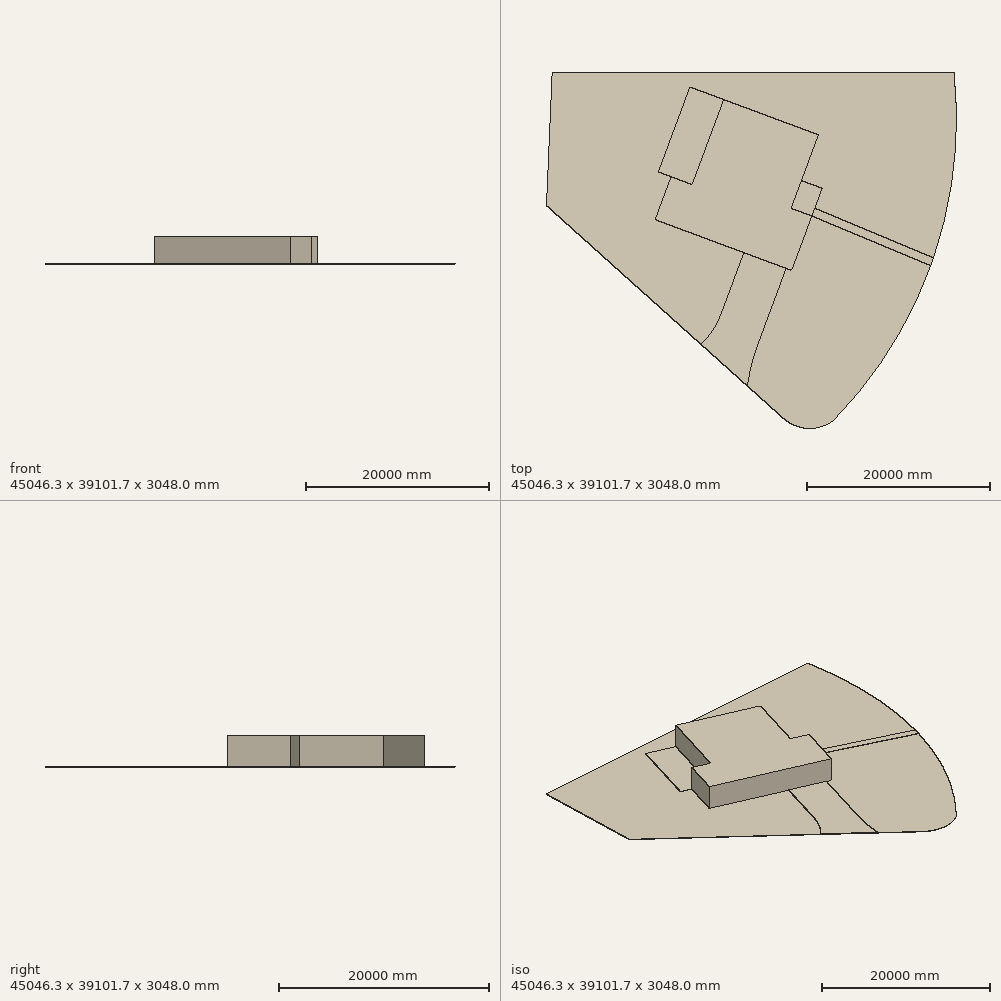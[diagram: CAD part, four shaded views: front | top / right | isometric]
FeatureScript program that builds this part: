
annotation { "Feature Type Name" : "Feature", "Feature Type Description" : "" }
export const myFeature = defineFeature(function(context is Context, id is Id, definition is map)
    precondition{}
    {
        {
            var Q0;
            Q0=qCreatedBy(makeId("Top.planeOp"),FACE);
            var sketch = newSketch(context, id + "F0", { "sketchPlane" : qUnion([Q0])});
            skLineSegment(sketch, "E0", {"start": v(-19964.4, 0) * mm, "end": v(0, 0) * mm});
            skLineSegment(sketch, "E1", {"start": v(0, 0) * mm, "end": v(24180.8, 0) * mm});
            skLineSegment(sketch, "E2", {"start": v(-19964.4, 0) * mm, "end": v(-20508.97, -12713.74) * mm});
            skLineSegment(sketch, "E3", {"start": v(-20508.97, -12713.74) * mm, "end": v(-9941.45, -19665.7) * mm});
            skLineSegment(sketch, "E4", {"start": v(-9941.45, -19665.7) * mm, "end": v(-8642.36, -16165.19) * mm});
            skLineSegment(sketch, "E5", {"start": v(-8642.36, -16165.19) * mm, "end": v(6355.47, -21744.52) * mm});
            skLineSegment(sketch, "E6", {"start": v(6355.47, -21744.52) * mm, "end": v(8578.35, -15769.2) * mm});
            skLineSegment(sketch, "E7", {"start": v(8578.35, -15769.2) * mm, "end": v(6292.96, -14919.01) * mm});
            skLineSegment(sketch, "E8", {"start": v(6292.96, -14919.01) * mm, "end": v(9295.18, -6848.75) * mm});
            skLineSegment(sketch, "E9", {"start": v(9295.18, -6848.75) * mm, "end": v(-1108.08, -2978.64) * mm});
            skLineSegment(sketch, "E10", {"start": v(-1108.08, -2978.64) * mm, "end": v(-4579.67, -12310.62) * mm});
            skLineSegment(sketch, "E11", {"start": v(-4579.67, -12310.62) * mm, "end": v(-6888.86, -11451.58) * mm});
            skLineSegment(sketch, "E12", {"start": v(-6888.86, -11451.58) * mm, "end": v(-8642.36, -16165.19) * mm});
            skLineSegment(sketch, "E13", {"start": v(-1108.08, -2978.64) * mm, "end": v(-4821.83, -1597.09) * mm});
            skLineSegment(sketch, "E14", {"start": v(-4821.83, -1597.09) * mm, "end": v(-8293.42, -10929.07) * mm});
            skLineSegment(sketch, "E15", {"start": v(-8293.42, -10929.07) * mm, "end": v(-6888.86, -11451.58) * mm});
            skLineSegment(sketch, "E16", {"start": v(8578.35, -15769.2) * mm, "end": v(9711.93, -12722.02) * mm});
            skLineSegment(sketch, "E17", {"start": v(9711.93, -12722.02) * mm, "end": v(7426.54, -11871.83) * mm});
            skLineSegment(sketch, "E18", {"start": v(-20508.97, -12713.74) * mm, "end": v(-20590.49, -14617) * mm});
            skLineSegment(sketch, "E19", {"start": v(-20590.49, -14617) * mm, "end": v(-3584.3, -29893.43) * mm});
            skLineSegment(sketch, "E20", {"start": v(5748.41, -21518.7) * mm, "end": v(2604.5, -29969.85) * mm});
            skLineSegment(sketch, "E21", {"start": v(1106.23, -19791.76) * mm, "end": v(-1417.76, -26576.5) * mm});
            skLineSegment(sketch, "E22", {"start": v(-3584.3, -29893.43) * mm, "end": v(1479.76, -34442.41) * mm});
            skLineSegment(sketch, "E23", {"start": v(1479.76, -34442.41) * mm, "end": v(5410.07, -37972.97) * mm});
            skLineSegment(sketch, "E24", {"start": v(8578.35, -15769.2) * mm, "end": v(21631.46, -21225.98) * mm});
            skLineSegment(sketch, "E25", {"start": v(8897.42, -14911.5) * mm, "end": v(21934.45, -20361.56) * mm});
            skLineSegment(sketch, "E26", {"start": v(-1108.08, -2978.64) * mm, "end": v(0, 0) * mm});
            skLineSegment(sketch, "E27", {"start": v(24180.8, 0) * mm, "end": v(21934.45, -20361.56) * mm, "construction": true});
            skLineSegment(sketch, "E28", {"start": v(21631.46, -21225.98) * mm, "end": v(10938.6, -38265.6) * mm, "construction": true});
            skArc(sketch, "E29", {"start": v(10938.6, -38265.6) * mm, "mid": v(21847.05, -20616.48) * mm, "end": v(24180.8, 0) * mm});
            skArc(sketch, "E30", {"start": v(5410.07, -37972.97) * mm, "mid": v(8122.66, -39095.53) * mm, "end": v(10938.6, -38265.6) * mm});
            skArc(sketch, "E31", {"start": v(2604.5, -29969.85) * mm, "mid": v(1919.26, -32175.23) * mm, "end": v(1479.76, -34442.41) * mm});
            skArc(sketch, "E32", {"start": v(-3584.3, -29893.43) * mm, "mid": v(-2315.8, -28355.95) * mm, "end": v(-1417.76, -26576.5) * mm});
            skLineSegment(sketch, "E33", {"start": v(-9941.45, -19665.7) * mm, "end": v(-11198.7, -23053.52) * mm, "construction": true});
            skSolve(sketch);
        }
        {
            var Q0;
            {var subQ8=sQuery(id+"F0.wireOp",EDGE,"E6");Q0=makeQuery(id+"F0.imprint","IMPRINT",FACE,{"disambiguationData":[TD([[makeQuery(id+"F0.imprint","IMPRINT",EDGE,{"derivedFrom":subQ8}),1.0]])]});}
            extrude(context, id + "F1", {"entities" : qUnion([Q0]), "depth" : 3048 * mm, "offsetDistance" : 30.48 * mm});
        }
        {
            var Q0;
            {var subQ1=sQuery(id+"F0.wireOp",EDGE,"E20");Q0=makeQuery(id+"F0.imprint","IMPRINT",FACE,{"disambiguationData":[TD([[makeQuery(id+"F0.imprint","IMPRINT",EDGE,{"derivedFrom":subQ1}),-1.0]])]});}
            var Q1;
            {var subQ0=sQuery(id+"F0.wireOp",EDGE,"E24");Q1=makeQuery(id+"F0.imprint","IMPRINT",FACE,{"disambiguationData":[TD([[makeQuery(id+"F0.imprint","IMPRINT",EDGE,{"derivedFrom":subQ0}),1.0]])]});}
            var Q2;
            Q2=makeQuery(id+"F0.imprint","IMPRINT",FACE,{"disambiguationData":[TD([[makeQuery(id+"F0.imprint","IMPRINT",EDGE,{"derivedFrom":sQuery(id+"F0.wireOp",EDGE,"E10")}),-1.0]])]});
            extrude(context, id + "F2", {"entities" : qUnion([Q0, Q1, Q2]), "depth" : 101.6 * mm, "offsetDistance" : 30.48 * mm});
        }
        {
            var Q0;
            Q0=makeQuery(id+"F0.imprint","IMPRINT",FACE,{"disambiguationData":[TD([[makeQuery(id+"F0.imprint","IMPRINT",EDGE,{"derivedFrom":sQuery(id+"F0.wireOp",EDGE,"E0")}),-1.0]])]});
            var Q1;
            {var subQ4=sQuery(id+"F0.wireOp",EDGE,"E1");Q1=makeQuery(id+"F0.imprint","IMPRINT",FACE,{"disambiguationData":[TD([[makeQuery(id+"F0.imprint","IMPRINT",EDGE,{"derivedFrom":subQ4}),-1.0]])]});}
            var Q2;
            {var subQ1=sQuery(id+"F0.wireOp",EDGE,"E6");Q2=makeQuery(id+"F0.imprint","IMPRINT",FACE,{"disambiguationData":[TD([[makeQuery(id+"F0.imprint","IMPRINT",EDGE,{"derivedFrom":subQ1}),-1.0]])]});}
            var Q3;
            Q3=makeQuery(id+"F0.imprint","IMPRINT",FACE,{"disambiguationData":[TD([[makeQuery(id+"F0.imprint","IMPRINT",EDGE,{"derivedFrom":sQuery(id+"F0.wireOp",EDGE,"E3")}),-1.0]])]});
            extrude(context, id + "F3", {"entities" : qUnion([Q0, Q1, Q2, Q3]), "depth" : 50.8 * mm, "offsetDistance" : 30.48 * mm});
        }
        {
            var Q0;
            {var subQ3=sQuery(id+"F0.wireOp",EDGE,"E7");Q0=makeQuery(id+"F0.imprint","IMPRINT",FACE,{"disambiguationData":[TD([[makeQuery(id+"F0.imprint","IMPRINT",EDGE,{"derivedFrom":subQ3}),-1.0]])]});}
            extrude(context, id + "F4", {"entities" : qUnion([Q0]), "depth" : 50.8 * mm, "offsetDistance" : 30.48 * mm});
        }
    });
